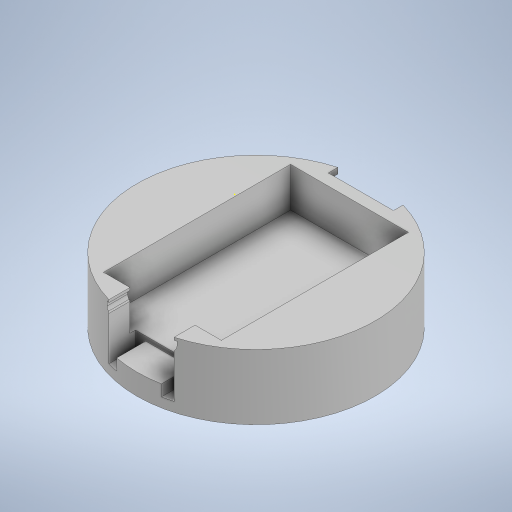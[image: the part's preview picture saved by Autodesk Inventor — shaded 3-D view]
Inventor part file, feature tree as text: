
AUTODESK INVENTOR PART (.ipt)
format: ipt  version: 2023 (Build 270158000, 158)  size: 635,392 bytes
history: mixed  units: in
note: dims shown in document units (in); Inventor stores cm internally (conversion verified against a paired STEP export)
features: extrude x17, sketch x15, projected_geometry x4, move_body x2, fillet x1, other x1, imported_body x1
ambient origin geometry x8: Origin, YZ Plane, XZ Plane, XY Plane, X Axis, Y Axis, Z Axis, Center Point
bodies: Solid1 (imported_parasolid)
feature tree (41):
  sketch  "Sketch4"  dims[d2=0.2313in d3=0.0in d4=0.0787in d5=0.0in]
  extrude  "Extrusion1"  Depth=0.0787in TaperAngle=0.0deg
  extrude  "Extrusion2"  Depth=0.3937in TaperAngle=0.0deg
  extrude  "Extrusion3"  Depth=0.4528in
  extrude  "Extrusion4"  Depth=0.3937in TaperAngle=0.0deg
  extrude  "Extrusion8"  Depth=0.0394in
  extrude  "Extrusion9"  Depth=0.0472in
  extrude  "Extrusion10"  Depth=0.2894in TaperAngle=0.0deg
  sketch  "Sketch14"  dims[d31=0.0591in d32=0.2894in d33=0.0in]
  extrude  "Extrusion14"  Depth=0.2185in
  extrude  "Extrusion15"  Depth=0.3937in TaperAngle=0.0deg
  extrude  "Extrusion17"  Depth=0.0097in
  extrude  "Extrusion18"  Depth=0.0236in
  sketch  "Sketch20"  dims[d55=0.0097in d56=0.0236in]
  extrude  "Extrusion19"  Depth=0.0185in
  fillet  "Fillet1"  Radius=0.0185in
  sketch  "Sketch21"  dims[d59=0.8563in d60=0.0in d61=0.0295in d62=0.0185in]
  extrude  "Extrusion20"  Depth=0.0787in
  extrude  "Extrusion21"  Depth=1.1811in
  extrude  "Extrusion22"  Depth=0.0394in TaperAngle=0.0deg
  extrude  "Extrusion23"  Depth=0.0197in
  extrude  "Extrusion24"  Depth=0.3937in
  move_body  "Move Body1"
  move_body  "Move Body2"
  sketch  "Sketch5"  dims[d6=0.0787in d7=0.0in d8=0.3937in d9=0.0in]
  sketch  "Sketch6"  dims[d16=0.4744in d20=0.4528in]
  sketch  "Sketch10"  dims[d21=0.0108in d22=0.3937in d23=0.0in]
  sketch  "Sketch11"  dims[d24=0.0394in d25=0.0in d27=0.0472in]
  projected_geometry  "Projected Loop1"
  sketch  "Sketch12"  dims[d28=0.0591in d29=0.0472in]
  sketch  "Sketch17"  dims[d38=0.437in d39=0.2185in]
  sketch  "Sketch18"  dims[d42=0.3937in d43=0.0in d44=0.3937in d45=0.0in]
  sketch  "Sketch19"  dims[d53=0.0259in d54=0.0097in]
  sketch  "Sketch22"  dims[d64=0.8563in d65=0.0in d66=0.0787in]
  projected_geometry  "Projected Loop2"
  sketch  "Sketch23"  dims[d67=0.0394in d68=1.1811in]
  projected_geometry  "Projected Loop3"
  sketch  "Sketch24"  dims[d69=0.5906in d70=0.0394in d71=0.0in d72=0.0197in d74=0.0118in d75=0.0118in d77=0.0in d78=0.311in d79=0.0787in d80=0.0787in d81=0.0787in d82=0.3937in d83=0.0in d84=0.1969in d85=0.0984in d86=0.3937in d87=0.1969in d88=0.8268in d89=0.0197in d90=0.0in d91=0.0197in d92=0.0in d93=0.3937in d94=0.0in d95=0.0591in d96=0.0in d97=90.0deg d98=-0.6184in d63=0.0in]
  projected_geometry  "Projected Loop4"
  other  "Btm"
  imported_body  NMx_Import_Brep_tag  [imported B-rep: ~36 faces, bbox_mm=[30.0, 10.0, 40.394925]]
